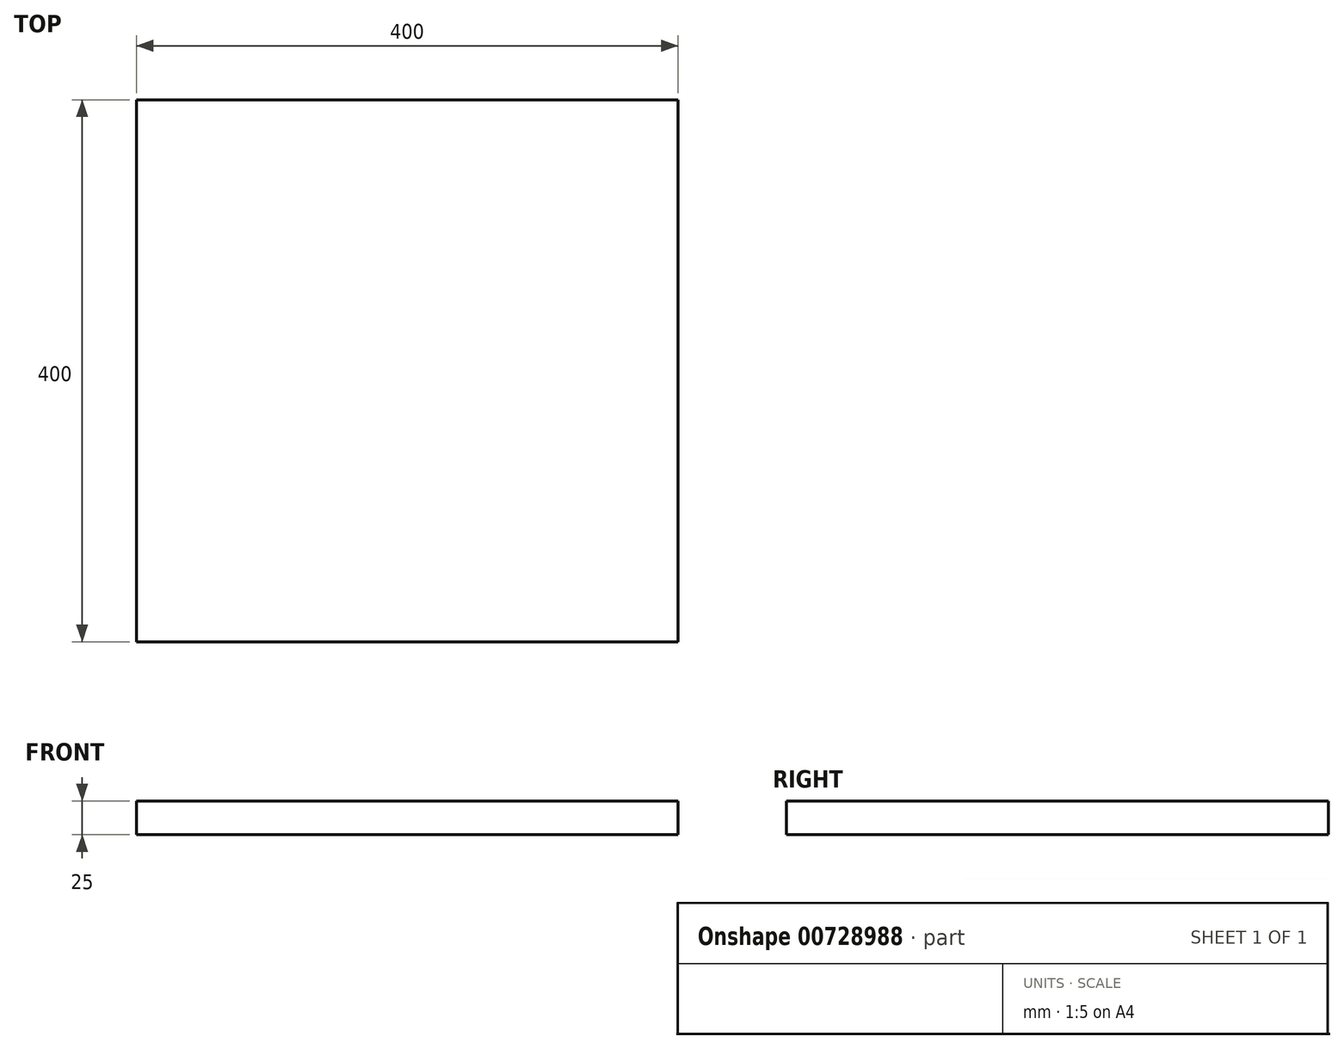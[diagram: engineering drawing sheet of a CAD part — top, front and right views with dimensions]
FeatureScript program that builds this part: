
annotation { "Feature Type Name" : "Feature", "Feature Type Description" : "" }
export const myFeature = defineFeature(function(context is Context, id is Id, definition is map)
    precondition{}
    {
        {
            var Q0;
            Q0=qCreatedBy(makeId("Top.planeOp"),FACE);
            var sketch = newSketch(context, id + "F0", { "sketchPlane" : qUnion([Q0])});
            skLineSegment(sketch, "E0.bottom", {"start": v(200, 200) * mm, "end": v(-200, 200) * mm});
            skLineSegment(sketch, "E0.top", {"start": v(200, -200) * mm, "end": v(-200, -200) * mm});
            skLineSegment(sketch, "E0.left", {"start": v(200, 200) * mm, "end": v(200, -200) * mm});
            skLineSegment(sketch, "E0.right", {"start": v(-200, 200) * mm, "end": v(-200, -200) * mm});
            skPoint(sketch, "E0.middle", {"position": v(0, 0) * mm});
            skSolve(sketch);
        }
        {
            var Q0;
            Q0=makeQuery(id+"F0.imprint","IMPRINT",FACE,{"disambiguationData":[TD([[makeQuery(id+"F0.imprint","IMPRINT",EDGE,{"derivedFrom":sQuery(id+"F0.wireOp",EDGE,"E0.bottom")}),1.0]])]});
            extrude(context, id + "F1", {"entities" : qUnion([Q0]), "depth" : 25 * mm, "offsetDistance" : 25 * mm});
        }
    });
